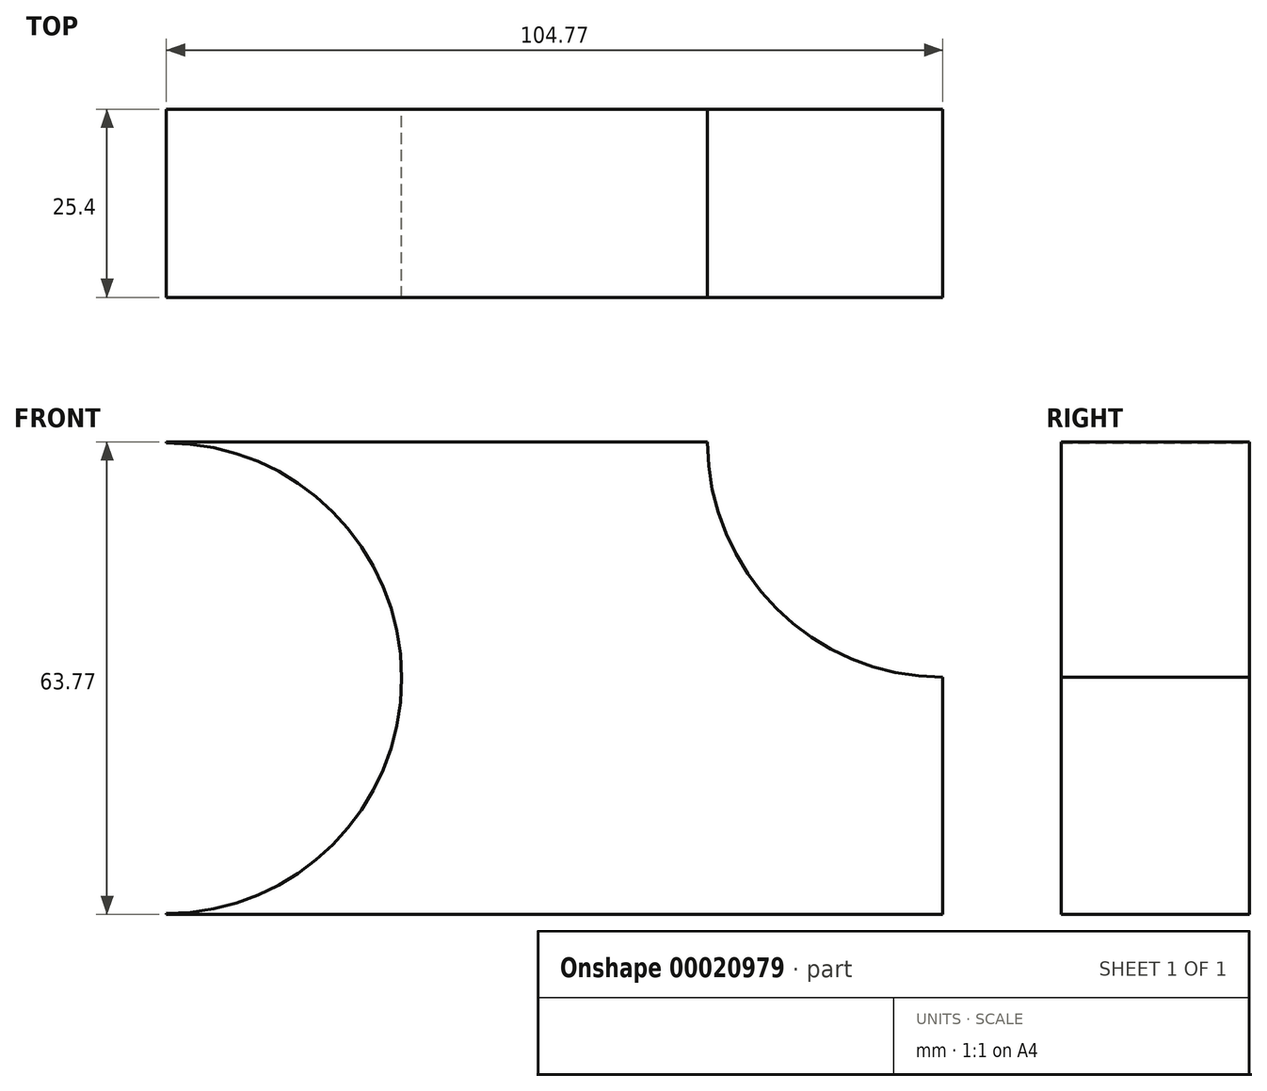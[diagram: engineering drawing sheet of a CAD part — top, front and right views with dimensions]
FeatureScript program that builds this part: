
annotation { "Feature Type Name" : "Feature", "Feature Type Description" : "" }
export const myFeature = defineFeature(function(context is Context, id is Id, definition is map)
    precondition{}
    {
        {
            var Q0;
            Q0=qCreatedBy(makeId("Front.planeOp"),FACE);
            var sketch = newSketch(context, id + "F0", { "sketchPlane" : qUnion([Q0])});
            skLineSegment(sketch, "E0.bottom", {"start": v(-63.15, 30.16) * mm, "end": v(9.87, 30.16) * mm});
            skLineSegment(sketch, "E0.top", {"start": v(-63.15, -33.61) * mm, "end": v(41.62, -33.61) * mm});
            skLineSegment(sketch, "E0.left", {"start": v(-63.15, 30.16) * mm, "end": v(-63.15, -33.61) * mm});
            skLineSegment(sketch, "E0.right", {"start": v(41.62, -1.6) * mm, "end": v(41.62, -33.61) * mm});
            skCircle(sketch, "E1", {"center": v(-63.15, -1.73) * mm, "radius": 31.75 * mm});
            skCircle(sketch, "E2", {"center": v(-63.15, -1.73) * mm, "radius": 12.7 * mm});
            skArc(sketch, "E3", {"start": v(9.87, 30.16) * mm, "mid": v(19.17, 7.7) * mm, "end": v(41.62, -1.6) * mm});
            skSolve(sketch);
        }
        {
            var Q0;
            {var subQ1=sQuery(id+"F0.wireOp",EDGE,"E0.left");var subQ4=sQuery(id+"F0.wireOp",EDGE,"E1");var subQ6=makeQuery(id+"F0.imprint","INTERSECT",VERTEX,{"disambiguationData":[OD(0.0)],"derivedFrom":[subQ1,subQ4]});Q0=makeQuery(id+"F0.imprint","IMPRINT",FACE,{"disambiguationData":[TD([[makeQuery(id+"F0.imprint","IMPRINT",EDGE,{"disambiguationData":[TD([[subQ6,-1.0]])],"derivedFrom":subQ1}),-1.0]])]});}
            var Q1;
            {var subQ1=sQuery(id+"F0.wireOp",EDGE,"E0.left");var subQ4=sQuery(id+"F0.wireOp",EDGE,"E1");var subQ6=makeQuery(id+"F0.imprint","INTERSECT",VERTEX,{"disambiguationData":[OD(0.0)],"derivedFrom":[subQ1,subQ4]});Q1=makeQuery(id+"F0.imprint","IMPRINT",FACE,{"disambiguationData":[TD([[makeQuery(id+"F0.imprint","IMPRINT",EDGE,{"disambiguationData":[TD([[subQ6,-1.0]])],"derivedFrom":subQ1}),1.0]])]});}
            var Q2;
            {var subQ5=sQuery(id+"F0.wireOp",EDGE,"E0.bottom");Q2=makeQuery(id+"F0.imprint","IMPRINT",FACE,{"disambiguationData":[TD([[makeQuery(id+"F0.imprint","IMPRINT",EDGE,{"derivedFrom":subQ5}),-1.0]])]});}
            extrude(context, id + "F1", {"entities" : qUnion([Q0, Q1, Q2]), "depth" : 25.4 * mm});
        }
    });
